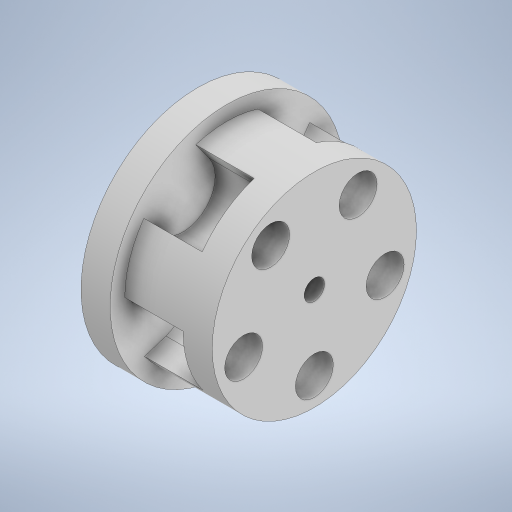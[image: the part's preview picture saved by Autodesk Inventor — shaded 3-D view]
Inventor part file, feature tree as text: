
AUTODESK INVENTOR PART (.ipt)
format: ipt  version: 2023 (Build 270158000, 158)  size: 349,184 bytes
history: native  units: mm
features: extrude x3, sketch x3
ambient origin geometry x8: Origin, YZ Plane, XZ Plane, XY Plane, X Axis, Y Axis, Z Axis, Center Point
bodies: Solid1 (feature_tree)
feature tree (6):
  extrude  "Extrusion1"  Depth=3.5mm
  extrude  "Extrusion2"  Depth=3.5mm
  extrude  "Extrusion3"  Depth=5.0mm TaperAngle=0.0deg
  sketch  "Sketch1"  dims[d0=30.0mm d1=3.5mm]
  sketch  "Sketch2"  dims[d2=40.0mm d4=360.0deg d6=3.5mm]
  sketch  "Sketch3"  dims[d7=40.0mm d8=5.0mm d9=0.0mm d10=25.5mm d11=6.5mm d12=50.0mm d14=360.0deg d16=35.0mm d17=15.0mm d18=0.0mm d19=11.0mm d20=50.0mm d22=360.0deg d24=10.0mm d25=0.0mm]
